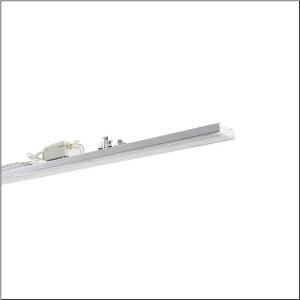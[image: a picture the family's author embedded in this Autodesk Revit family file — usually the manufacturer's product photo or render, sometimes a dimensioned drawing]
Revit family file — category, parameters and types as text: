
# Revit family: licross_r__21_recessed_mo_52tl12dn4axg3s4_bc26
name_source: partatom
category: Lighting Fixtures
units: mm (PartAtom-declared; Revit-internal decimal feet)

## family parameters
Cut with Voids When Loaded = No
Host = Face
Light Source = No
Part Type = Normal
Room Calculation Point = No
Round Connector Dimension = Use Diameter
Shared = No

## types (1)
- --- (1 x LED, 950 lm, 6.7 W, 4000K)
    Apparent Load = 7 VA
    CIE Flux Codes = 72 92 99 100 100
    Color Rendering = 80
    Color Temperature = 4000K
    Default Elevation = 1800 mm
    Description = Licross® 21 Recessed MO, luminaire insert, of sheet steel, galvanised, coil coated, white, length: 1.500mm, width: 66mm, height: 67mm, LED rated luminous flux: 10.280lm, light colour: 840, control gear: DALI 2, with plug, 6-pole, with phase selection, for trunking rail, 9 or 11-core, mains connection: 220..240V, AC, 50/60Hz, rated input power: 62W, for trunking rail, 9-/11-core, halogen-free wiring, for emergency light function, converter,control gear: single battery element, battery: LiFeP04, 9Ah, primary optical cover: cover, of PMMA, light emission: direct distribution, primary light characteristic: symmetric, protection rating (complete): IP40, insulation class (complete): insulation class I (protective earthing), certification: CE, UKCA, protection symbol: D if used in an environment without relevant dust loads with corresponding accessories, impact resistance: IK06, permissible ambient temperature for indoor applications: +5..+35°C, standard: EN 60598-2-22, LABS conformity tested according to VDMA 24364:2018-05, reducing of maximum allowable ambient temperature of 5°C with ceiling mounting, corresponds to IFS (International Featured Standards) requirements for safety and quality in the food industry, packaging unit: 1 piece
    Height = 58 mm
    Lamp = 1 x LED
    Lamp Light Flux = 950 lm
    Lamp Power = 6.7 W
    Lamp count = 1
    Length = 1500 mm
    Luminous efficacy = 142 lm/W
    Manufacturer = Siteco
    ModVariant = No
    Model = 52TL12DN4AXG3S4
    Mounting Place = Ceiling
    Mounting Type = Pendant
    Number of Poles = 1
    OnlyDefault = Yes
    Power Factor = 1
    Product Name = Licross® 21 Recessed MO
    Product group = luminaire insert
    ProductGroupID = 901
    Protection Class = Protection class I
    Protection Degree = IP 40
    RLX_Detail_Level = 1
    RLX_Emergency_Light_Flux = 0 lm
    RLX_Emergency_Type = 0
    RLX_Emergency_Type_DB = No
    RlxData = <blob elided: 25021 chars, md5=6eb3d411>
    Socket = socket
    Standby Power = 0 W
    System Light Flux = 950 lm
    System Power = 7 W
    Type Comments = : emergency light operation: 3 h
    Type Image = l_1296930.jpg
    URL = http://relux.com
    VarID = @adj_040179
    Voltage = 0 V
    Weight = 0.00 kg
    Width = 66 mm

## geometry (parser evidence)
native form markers: Blend x4, Sweep x11
no freeform markers — native parametric forms only
